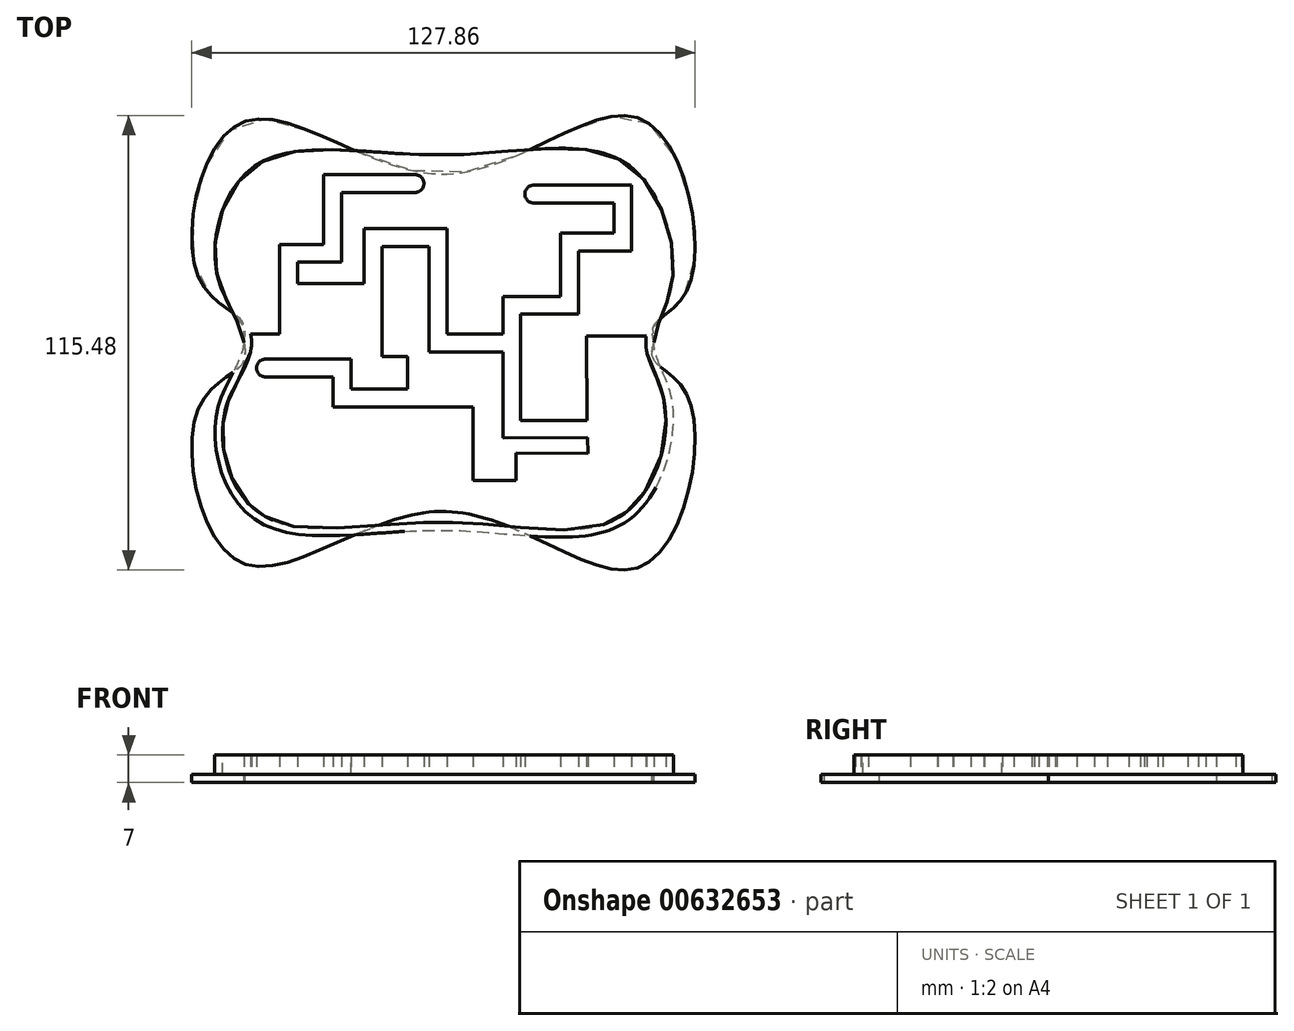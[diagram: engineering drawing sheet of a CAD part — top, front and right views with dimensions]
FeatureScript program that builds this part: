
annotation { "Feature Type Name" : "Feature", "Feature Type Description" : "" }
export const myFeature = defineFeature(function(context is Context, id is Id, definition is map)
    precondition{}
    {
        {
            var Q0;
            Q0=qCreatedBy(makeId("Top.planeOp"),FACE);
            var sketch = newSketch(context, id + "F0", { "sketchPlane" : qUnion([Q0])});
            skFitSpline(sketch, "E0", {"points": [v(-50.95, 0) * mm, v(-57.89, 18) * mm, v(-47.79, 45.14) * mm, v(0, 47.66) * mm, v(46.27, 45.45) * mm, v(57.95, 15.47) * mm, v(53.2, 0) * mm], "startDerivative": vector(-12.65, 126.2) * mm, "endDerivative": vector(0, -109.52) * mm});
            skFitSpline(sketch, "E1.MirrorCS", {"points": [v(-50.95, 0) * mm, v(-57.89, -18) * mm, v(-47.79, -45.14) * mm, v(0, -47.66) * mm, v(46.27, -45.45) * mm, v(57.95, -15.47) * mm, v(53.2, 0) * mm], "startDerivative": vector(-12.65, -126.2) * mm, "endDerivative": vector(0, 109.52) * mm});
            skFitSpline(sketch, "E2.0", {"points": [v(-48.96, 0.2) * mm, v(-49.03, 0.98) * mm, v(-49.33, 2.5) * mm, v(-50.33, 5.37) * mm, v(-51.7, 8.07) * mm, v(-53.12, 10.8) * mm, v(-54.13, 12.87) * mm, v(-55.02, 15.01) * mm, v(-55.6, 16.88) * mm, v(-55.95, 18.44) * mm, v(-56.21, 20.07) * mm, v(-56.37, 22.22) * mm, v(-56.3, 24.94) * mm, v(-55.95, 27.7) * mm, v(-55.33, 30.48) * mm, v(-54.16, 34.1) * mm, v(-52.47, 37.46) * mm, v(-50.3, 40.34) * mm, v(-48.77, 41.9) * mm, v(-47.42, 42.97) * mm, v(-46.37, 43.7) * mm, v(-45.24, 44.33) * mm, v(-42.86, 45.45) * mm, v(-38.76, 46.58) * mm, v(-32.3, 47.13) * mm, v(-25.08, 46.98) * mm, v(-17.3, 46.44) * mm, v(-10.49, 45.95) * mm, v(-4.94, 45.7) * mm, v(-1.45, 45.64) * mm, v(1.35, 45.67) * mm, v(4.13, 45.76) * mm, v(7.57, 45.94) * mm, v(11.64, 46.25) * mm, v(16.95, 46.7) * mm, v(23.34, 47.25) * mm, v(30.44, 47.52) * mm, v(36.81, 47.08) * mm, v(41.36, 45.87) * mm, v(44.12, 44.48) * mm, v(45.57, 43.52) * mm, v(46.97, 42.42) * mm, v(48.6, 40.82) * mm, v(50.96, 37.82) * mm, v(53.37, 33.4) * mm, v(55.33, 27.52) * mm, v(56.12, 22.59) * mm, v(56.25, 18.88) * mm, v(56.11, 16.73) * mm, v(55.88, 15.14) * mm, v(55.57, 13.63) * mm, v(55.05, 11.83) * mm, v(54.3, 9.81) * mm, v(53.47, 7.88) * mm, v(52.65, 5.98) * mm, v(51.92, 4.08) * mm, v(51.37, 2.11) * mm, v(51.2, 0.72) * mm, v(51.2, 0) * mm]});
            skFitSpline(sketch, "E3.0", {"points": [v(-48.96, -0.2) * mm, v(-49.03, -0.98) * mm, v(-49.33, -2.5) * mm, v(-50.33, -5.37) * mm, v(-51.7, -8.07) * mm, v(-53.12, -10.8) * mm, v(-54.13, -12.87) * mm, v(-55.02, -15.01) * mm, v(-55.6, -16.88) * mm, v(-55.95, -18.44) * mm, v(-56.21, -20.07) * mm, v(-56.37, -22.22) * mm, v(-56.3, -24.94) * mm, v(-55.95, -27.7) * mm, v(-55.33, -30.48) * mm, v(-54.16, -34.1) * mm, v(-52.47, -37.46) * mm, v(-50.3, -40.34) * mm, v(-48.77, -41.9) * mm, v(-47.42, -42.97) * mm, v(-46.37, -43.7) * mm, v(-45.24, -44.33) * mm, v(-42.86, -45.45) * mm, v(-38.76, -46.58) * mm, v(-32.3, -47.13) * mm, v(-25.08, -46.98) * mm, v(-17.3, -46.44) * mm, v(-10.49, -45.95) * mm, v(-4.94, -45.7) * mm, v(-1.45, -45.64) * mm, v(1.35, -45.67) * mm, v(4.13, -45.76) * mm, v(7.57, -45.94) * mm, v(11.64, -46.25) * mm, v(16.95, -46.7) * mm, v(23.34, -47.25) * mm, v(30.44, -47.52) * mm, v(36.81, -47.08) * mm, v(41.36, -45.87) * mm, v(44.12, -44.48) * mm, v(45.57, -43.52) * mm, v(46.97, -42.42) * mm, v(48.6, -40.82) * mm, v(50.96, -37.82) * mm, v(53.37, -33.4) * mm, v(55.33, -27.52) * mm, v(56.12, -22.59) * mm, v(56.25, -18.88) * mm, v(56.11, -16.73) * mm, v(55.88, -15.14) * mm, v(55.57, -13.63) * mm, v(55.05, -11.83) * mm, v(54.3, -9.81) * mm, v(53.47, -7.88) * mm, v(52.65, -5.98) * mm, v(51.92, -4.08) * mm, v(51.37, -2.11) * mm, v(51.2, -0.72) * mm, v(51.2, 0) * mm]});
            skLineSegment(sketch, "E4", {"start": v(-37.36, 14.99) * mm, "end": v(-20.4, 14.99) * mm});
            skLineSegment(sketch, "E5", {"start": v(-20.4, 14.99) * mm, "end": v(-20.4, 29.05) * mm});
            skLineSegment(sketch, "E6", {"start": v(-20.4, 29.05) * mm, "end": v(0.62, 29.05) * mm});
            skLineSegment(sketch, "E7", {"start": v(0.62, 29.05) * mm, "end": v(0.62, 2.17) * mm});
            skLineSegment(sketch, "E8", {"start": v(19.37, 2.17) * mm, "end": v(19.37, -19.5) * mm});
            skLineSegment(sketch, "E9.0", {"start": v(-49.37, -2.33) * mm, "end": v(-30.44, -2.33) * mm});
            skLineSegment(sketch, "E10.0", {"start": v(-30.44, -2.33) * mm, "end": v(-30.44, 10.32) * mm});
            skLineSegment(sketch, "E11.0", {"start": v(40.68, -2.76) * mm, "end": v(51.67, -2.76) * mm});
            skLineSegment(sketch, "E11.1", {"start": v(-15.8, 10.49) * mm, "end": v(-15.8, 24.45) * mm});
            skLineSegment(sketch, "E11.4", {"start": v(-49.46, -2.33) * mm, "end": v(-30.44, -2.33) * mm});
            skLineSegment(sketch, "E11.5", {"start": v(-15.8, 24.45) * mm, "end": v(-3.88, 24.45) * mm});
            skLineSegment(sketch, "E11.6", {"start": v(-3.88, 24.45) * mm, "end": v(-3.88, -2.43) * mm});
            skLineSegment(sketch, "E11.7", {"start": v(-3.88, -2.43) * mm, "end": v(14.87, -2.43) * mm});
            skLineSegment(sketch, "E11.8", {"start": v(14.87, -2.43) * mm, "end": v(14.87, -24.2) * mm});
            skLineSegment(sketch, "E12", {"start": v(-37.36, 14.99) * mm, "end": v(-37.36, 20.48) * mm});
            skLineSegment(sketch, "E13", {"start": v(-37.36, 20.48) * mm, "end": v(-26.16, 20.48) * mm});
            skLineSegment(sketch, "E14", {"start": v(-26.16, 20.48) * mm, "end": v(-26.16, 38.19) * mm});
            skLineSegment(sketch, "E15", {"start": v(-26.16, 38.19) * mm, "end": v(-7.45, 38.19) * mm});
            skLineSegment(sketch, "E16.0", {"start": v(-41.86, 14.99) * mm, "end": v(-41.86, 24.98) * mm});
            skLineSegment(sketch, "E17", {"start": v(-41.86, 14.99) * mm, "end": v(-41.86, 2.17) * mm});
            skLineSegment(sketch, "E18.0", {"start": v(-41.86, 24.98) * mm, "end": v(-30.66, 24.98) * mm});
            skLineSegment(sketch, "E19.0", {"start": v(-30.66, 24.98) * mm, "end": v(-30.66, 42.69) * mm});
            skLineSegment(sketch, "E20.0", {"start": v(-30.66, 42.69) * mm, "end": v(-7.45, 42.69) * mm});
            skArc(sketch, "E21", {"start": v(-7.45, 42.69) * mm, "mid": v(-5.2, 40.44) * mm, "end": v(-7.45, 38.19) * mm});
            skLineSegment(sketch, "E22", {"start": v(-41.86, 2.17) * mm, "end": v(-49.3, 2.17) * mm});
            skLineSegment(sketch, "E23", {"start": v(-15.8, 10.49) * mm, "end": v(-15.8, -3.55) * mm});
            skLineSegment(sketch, "E24", {"start": v(-15.8, -3.55) * mm, "end": v(-9.3, -3.55) * mm});
            skLineSegment(sketch, "E25", {"start": v(-9.3, -3.55) * mm, "end": v(-9.3, -11.72) * mm});
            skLineSegment(sketch, "E26", {"start": v(-28.28, -16.3) * mm, "end": v(-28.28, -8.7) * mm});
            skLineSegment(sketch, "E27", {"start": v(-28.28, -8.7) * mm, "end": v(-45.48, -8.7) * mm});
            skLineSegment(sketch, "E28", {"start": v(-30.44, 10.32) * mm, "end": v(-20.3, 10.32) * mm});
            skLineSegment(sketch, "E29", {"start": v(-20.3, 10.32) * mm, "end": v(-20.3, -8.05) * mm});
            skLineSegment(sketch, "E30", {"start": v(-13.76, -8.05) * mm, "end": v(-13.76, -11.74) * mm});
            skLineSegment(sketch, "E31.0", {"start": v(-13.76, -11.74) * mm, "end": v(-23.78, -11.78) * mm});
            skLineSegment(sketch, "E32.0", {"start": v(-23.78, -4.2) * mm, "end": v(-45.48, -4.2) * mm});
            skLineSegment(sketch, "E32.1", {"start": v(-23.78, -11.78) * mm, "end": v(-23.78, -4.2) * mm});
            skLineSegment(sketch, "E32.2", {"start": v(-13.75, -11.74) * mm, "end": v(-23.78, -11.78) * mm});
            skLineSegment(sketch, "E32.4", {"start": v(19.37, 2.17) * mm, "end": v(19.37, -19.7) * mm});
            skLineSegment(sketch, "E32.5", {"start": v(19.37, -19.7) * mm, "end": v(36.28, -19.72) * mm});
            skLineSegment(sketch, "E32.9", {"start": v(0.62, 28.95) * mm, "end": v(0.62, 2.07) * mm});
            skLineSegment(sketch, "E32.10", {"start": v(-20.3, 28.95) * mm, "end": v(0.62, 28.95) * mm});
            skLineSegment(sketch, "E32.13", {"start": v(-20.3, -8.05) * mm, "end": v(-13.75, -8.05) * mm});
            skArc(sketch, "E33", {"start": v(-45.48, -8.7) * mm, "mid": v(-47.73, -6.44) * mm, "end": v(-45.48, -4.2) * mm});
            skLineSegment(sketch, "E34", {"start": v(19.37, 2.17) * mm, "end": v(19.37, 7.25) * mm});
            skLineSegment(sketch, "E35", {"start": v(19.37, 7.25) * mm, "end": v(34.02, 7.25) * mm});
            skLineSegment(sketch, "E36", {"start": v(34.02, 7.25) * mm, "end": v(34.02, 23.33) * mm});
            skLineSegment(sketch, "E37", {"start": v(34.02, 23.33) * mm, "end": v(47.58, 23.33) * mm});
            skLineSegment(sketch, "E38", {"start": v(47.58, 23.33) * mm, "end": v(47.58, 40) * mm});
            skLineSegment(sketch, "E39", {"start": v(47.58, 40) * mm, "end": v(22.68, 40) * mm});
            skLineSegment(sketch, "E40.0", {"start": v(14.87, 2.17) * mm, "end": v(14.87, 11.75) * mm});
            skLineSegment(sketch, "E41", {"start": v(0.62, 2.17) * mm, "end": v(14.87, 2.17) * mm});
            skLineSegment(sketch, "E42.0", {"start": v(43.08, 35.5) * mm, "end": v(22.68, 35.5) * mm});
            skLineSegment(sketch, "E42.1", {"start": v(43.08, 27.83) * mm, "end": v(43.08, 35.5) * mm});
            skLineSegment(sketch, "E42.3", {"start": v(29.52, 11.75) * mm, "end": v(29.52, 27.83) * mm});
            skLineSegment(sketch, "E42.4", {"start": v(14.87, 11.75) * mm, "end": v(29.52, 11.75) * mm});
            skLineSegment(sketch, "E43", {"start": v(29.52, 27.83) * mm, "end": v(43.08, 27.83) * mm});
            skArc(sketch, "E44", {"start": v(22.68, 35.5) * mm, "mid": v(20.43, 37.75) * mm, "end": v(22.68, 40) * mm});
            skLineSegment(sketch, "E45", {"start": v(40.65, -31.34) * mm, "end": v(22.7, -31.34) * mm});
            skLineSegment(sketch, "E46", {"start": v(22.7, -31.34) * mm, "end": v(22.7, -39.48) * mm});
            skLineSegment(sketch, "E47", {"start": v(22.7, -39.48) * mm, "end": v(2.83, -39.48) * mm});
            skLineSegment(sketch, "E48", {"start": v(2.83, -39.48) * mm, "end": v(2.83, -20.8) * mm});
            skLineSegment(sketch, "E49", {"start": v(2.83, -20.8) * mm, "end": v(-18.84, -20.8) * mm});
            skLineSegment(sketch, "E50", {"start": v(-18.84, -20.8) * mm, "end": v(-18.84, -35.98) * mm});
            skLineSegment(sketch, "E51", {"start": v(-18.84, -35.98) * mm, "end": v(-43.7, -35.98) * mm});
            skLineSegment(sketch, "E52", {"start": v(-43.7, -35.98) * mm, "end": v(-43.7, -20.8) * mm});
            skLineSegment(sketch, "E53", {"start": v(36.3, -24.14) * mm, "end": v(14.87, -24.2) * mm});
            skLineSegment(sketch, "E54.0", {"start": v(-39.2, -31.48) * mm, "end": v(-39.2, -20.8) * mm});
            skLineSegment(sketch, "E54.4", {"start": v(36.15, 1.74) * mm, "end": v(51.67, 1.74) * mm});
            skLineSegment(sketch, "E54.5", {"start": v(18.2, -28.06) * mm, "end": v(18.2, -34.98) * mm});
            skLineSegment(sketch, "E54.6", {"start": v(18.2, -34.98) * mm, "end": v(7.33, -34.98) * mm});
            skLineSegment(sketch, "E54.7", {"start": v(7.33, -34.98) * mm, "end": v(7.33, -16.3) * mm});
            skLineSegment(sketch, "E54.8", {"start": v(7.33, -16.3) * mm, "end": v(-23.34, -16.3) * mm});
            skLineSegment(sketch, "E54.9", {"start": v(-23.34, -16.3) * mm, "end": v(-23.34, -31.48) * mm});
            skLineSegment(sketch, "E54.10", {"start": v(-23.34, -31.48) * mm, "end": v(-39.2, -31.48) * mm});
            skLineSegment(sketch, "E55", {"start": v(18.2, -28.06) * mm, "end": v(36.43, -28.11) * mm});
            skArc(sketch, "E56", {"start": v(-43.7, -20.8) * mm, "mid": v(-41.45, -18.55) * mm, "end": v(-39.2, -20.8) * mm});
            skLineSegment(sketch, "E57", {"start": v(-28.28, -16.3) * mm, "end": v(-23.34, -16.3) * mm});
            skLineSegment(sketch, "E58", {"start": v(40.68, -2.76) * mm, "end": v(40.65, -31.34) * mm});
            skLineSegment(sketch, "E59", {"start": v(36.28, -19.72) * mm, "end": v(36.15, 1.74) * mm});
            skLineSegment(sketch, "E60", {"start": v(36.3, -24.14) * mm, "end": v(36.43, -28.11) * mm});
            skLineSegment(sketch, "E61", {"start": v(-9.3, -11.72) * mm, "end": v(-13.75, -11.74) * mm});
            skLineSegment(sketch, "E62", {"start": v(51.2, 0.14) * mm, "end": v(51.2, 0) * mm});
            skLineSegment(sketch, "E63", {"start": v(-48.96, 0.2) * mm, "end": v(-48.96, -0.2) * mm});
            skSolve(sketch);
        }
        {
            var Q0;
            Q0 = qSketchRegion(id + "F0", true);
            var Q1;
            Q1=makeQuery(id+"F0.imprint","IMPRINT",FACE,{"disambiguationData":[TD([[makeQuery(id+"F0.imprint","IMPRINT",EDGE,{"derivedFrom":sQuery(id+"F0.wireOp",EDGE,"E11.1")}),-1.0]])]});
            var Q2;
            {var subQ5=sQuery(id+"F0.wireOp",EDGE,"E10.0");Q2=makeQuery(id+"F0.imprint","IMPRINT",FACE,{"disambiguationData":[TD([[makeQuery(id+"F0.imprint","IMPRINT",EDGE,{"derivedFrom":subQ5}),-1.0]])]});}
            var Q3;
            Q3=makeQuery(id+"F0.imprint","IMPRINT",FACE,{"disambiguationData":[TD([[makeQuery(id+"F0.imprint","IMPRINT",EDGE,{"derivedFrom":sQuery(id+"F0.wireOp",EDGE,"E4")}),1.0]])]});
            extrude(context, id + "F1", {"entities" : qUnion([Q0, Q1, Q2, Q3]), "depth" : 5 * mm, "offsetDistance" : 25 * mm});
        }
        {
            var Q0;
            Q0=qCreatedBy(makeId("Top.planeOp"),FACE);
            var sketch = newSketch(context, id + "F2", { "sketchPlane" : qUnion([Q0])});
            skFitSpline(sketch, "E64.1", {"points": [v(-50.95, 0) * mm, v(-51.5, -5.57) * mm, v(-62.51, -16.77) * mm, v(-51.64, -55.84) * mm, v(0.15, -42.88) * mm, v(50.21, -56.74) * mm, v(62.27, -14.76) * mm, v(53.2, -4.42) * mm, v(53.2, 0) * mm]});
            skFitSpline(sketch, "E65.0", {"points": [v(-50.95, 0) * mm, v(-51.5, 5.57) * mm, v(-62.51, 16.77) * mm, v(-51.64, 55.84) * mm, v(0.15, 42.88) * mm, v(50.21, 56.74) * mm, v(62.27, 14.76) * mm, v(53.2, 4.42) * mm, v(53.2, 0) * mm]});
            skPoint(sketch, "E64.0.end.orphan", {"position": v(51.2, 0.14) * mm});
            skPoint(sketch, "E64.0.start.orphan", {"position": v(-48.96, 0.2) * mm});
            skSolve(sketch);
        }
        {
            var Q0;
            Q0 = qSketchRegion(id + "F2", true);
            extrude(context, id + "F3", {"entities" : qUnion([Q0]), "operationType" : NewBodyOperationType.ADD, "oppositeDirection" : true, "depth" : 2 * mm, "offsetDistance" : 25 * mm});
        }
    });
